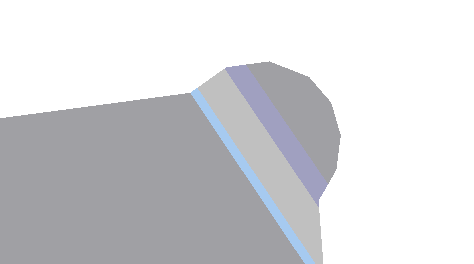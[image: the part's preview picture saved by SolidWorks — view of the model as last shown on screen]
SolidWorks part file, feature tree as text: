
SOLIDWORKS PART (.sldprt)
format: sldprt  version: not decoded by parser v0  size: 381,952 bytes
history: native  units: mm
features: sketch x9, thread x7, plane x3, hole x2, material x1, extrude x1, cut_extrude x1, cut_revolve x1 + 1 further entry (+7 scaffold rows collapsed)
feature tree (33):
  scaffold x7  (default folders/planes/origin — collapsed)
  material  "Matériau <non spécifié>"
  "Corps de surface"
  plane  "Plan de face"
  plane  "Plan de dessus"
  plane  "Plan de droite"
  sketch  "Esquisse1"  dims[D1=120.0mm D2=14.1mm]
  extrude  "BRUT"  Depth=25mm
  sketch  "Esquisse2"  dims[c1.D2=10.0mm c1.D1=79.4mm c1.D3=79.5mm c2.D3=40.0deg c2.D4=~107.080103mm c3.D4=40.0deg]
  sketch  "Esquisse3"  dims[D1=60.3mm]
  cut_extrude  "centrage"  Depth=2.4mm
  sketch  "Esquisse4"  dims[c1.D4=12.0mm c1.D1=48.0mm c1.D2=48.0mm c2.D2=120.0deg c2.D3=48.0mm c3.D3=120.0deg]
  hole  "Trou taraudé M10x1.51"  Diameter=8.5mm Depth=25mm
  sketch  "Esquisse3D2"
  sketch  "Esquisse6"  dims[hole-wizard template sketch: 59 standard entries collapsed; hole parameters kept: c18.Diamètre du trou pour taraudage jusqu'au prochain=8.5mm c18.Profondeur du trou pour taraudage jusqu'au prochain=25.0mm]
  thread  "Représentation de filetage1"  Diameter=10mm  [1 undecoded]
  thread  "Représentation de filetage2"  Diameter=10mm  [1 undecoded]
  thread  "Représentation de filetage3"  Diameter=10mm  [1 undecoded]
  thread  "Représentation de filetage4"  Diameter=10mm  [1 undecoded]
  hole  "Trou taraudé M12x1.751"  Diameter=10.2mm Depth=25mm
  sketch  "Esquisse3D3"
  sketch  "Esquisse7"  dims[hole-wizard template sketch: 59 standard entries collapsed; hole parameters kept: c18.Diamètre du trou pour taraudage jusqu'au prochain=10.2mm c18.Profondeur du trou pour taraudage jusqu'au prochain=25.0mm]
  thread  "Représentation de filetage5"  Diameter=12mm  [1 undecoded]
  thread  "Représentation de filetage6"  Diameter=12mm  [1 undecoded]
  thread  "Représentation de filetage7"  Diameter=12mm  [1 undecoded]
  sketch  "Esquisse10"  dims[D1=0.5mm]
  cut_revolve  "Enlèvement de matière-Révolution1"  Angle=360deg
decode coverage: 19 of 21 modeling features carry decoded parameters; 1 rows unclassified (native names shown)
note: ~ marks probable driven/reference dimensions
note: 7 parameter values undecoded
note: suppression state not decoded; provenance and decode notes live in map.json
